# Revit family: Grohe_WasteSet_29510KF0
name_source: partatom
category: Plumbing Fixtures
units: mm (PartAtom-declared; Revit-internal decimal feet)

## family parameters
Cut with Voids When Loaded = No
Host = Face
OmniClass Number = 23.45.05.00
OmniClass Title = Sanitary Equipment
Part Type = Normal
Room Calculation Point = No
Round Connector Dimension = Use Diameter
Shared = No

## types (1)
- Waste Set (29510KF0)
    Assembly Code = D2010
    AssetType = Fixed
    BIMObjectName = Grohe_WasteSet_29510KF0
    CO2NeutralProduction = GROHE is one of the first leading manufacturer within the sanitary industry having a CO2-neutral production.
    CW Connection = No
    ClassificationName = Uniclass2015
    ClassificationValue = Pr_70_55_96_97
    Color = Matt Black
    Cost = 0 $
    Default Elevation = 0 mm  [stored 0 ft]
    Description = Waste Set (29510KF0)
    DimensionsDocumentLink = https://cdn.cloud.grohe.com
    DocumentationCertificates = https://www.bimstore.co
    DocumentationInstallationGuide = https://www.bimstore.co
    DocumentationLiterature = https://www.bimstore.co
    DocumentationMaintenance = https://www.bimstore.co
    DocumentationTechnical = https://www.bimstore.co
    DurationUnit = Years
    EF000551 = 64 mm  [stored 0.209974 ft]
    EF005063 = TRUE
    EF008277 = Brass
    EF010904 = TRUE
    EF012637 = FALSE
    EF013612 = TRUE
    EF013617 = Other
    EF013618 = FALSE
    EF013619 = FALSE
    EF013621 = FALSE
    EF013632 = Brass
    EF013633 = Black
    EF013645 = TRUE
    EF020348 = TRUE
    EF020826 = TRUE
    EF021321 = FALSE
    EF022182 = FALSE
    EF022271 = FALSE
    EF022337 = Other
    EF022338 = External thread cylindrical BS
    EF022339 = 0
    EF025336 = FALSE
    Ecojoy = No
    ExpectedLife = 0
    FullRecyclabilityOfPlastic = All plastic components are fully recyclable
    GROHESocialCommittment = green.grohe.com/social_engagement
    GROHESustainability = green.grohe.com
    HW Connection = No
    IfcExportAs = IfcPipeFitting
    IfcExportType = IfcPipeFittingType
    Keynote = N13
    Manufacturer = Grohe
    ManufacturerName = Grohe
    Model = Waste Set (29510KF0)
    ModelNumber = 29510KF0
    ModelReference = Waste Set (29510KF0)
    NBSDescription = Washbasin wastes
    NBSObjectName = Grohe - Washbasin wastes
    NBSReference = 45-35-70/372
    NominalDepth = 0 mm  [stored 0 ft]
    NominalHeight = 0 mm  [stored 0 ft]
    NominalLength = 0 mm  [stored 0 ft]
    PrimaryMaterial = Grohe_MattBlack
    ProductDescription = with push-open cover

for wash basins with overflow

removable cover

closable

GROHE Long-Life Shine finish
    ProductNumber = 29510KF0
    ProductPageURL = https://www.grohe.co.uk
    ProductShortText = Waste set with push-open plug
    ProductType = Inlet-, Waste- +Overflow Fitti
    ProductionYear = 2023
    SustainabilityAward = green.grohe.com/awards
    SustainabilityReport = green.grohe.com/reporting
    Type Comments = Waste Set (29510KF0)
    TypeName = Waste Set (29510KF0)
    URL = https://www.grohe.co.uk
    Vent Connection = No
    WarrantyDurationLabor = 0
    WarrantyDurationParts = 0
    WarrantyDurationUnit = Years
    WasherOffsetMax = 70 mm  [stored 0.229659 ft]
    WasherOffsetMin = 20 mm  [stored 0.0656168 ft]
    Waste Connection = Yes
    _BSBibleVersion = 17
    _BimSpecGuid = 0
    _CurrentRevision = 1
    _DistributedBy = https://www.bimstore.co
    _ObjectUserGuide = https://www.bimstore.co

note: [stored X ft] marks values corroborated as IEEE doubles in the binary element streams (Revit-internal decimal feet)

## geometry (parser evidence)
native form markers: Sweep x2
no freeform markers — native parametric forms only
